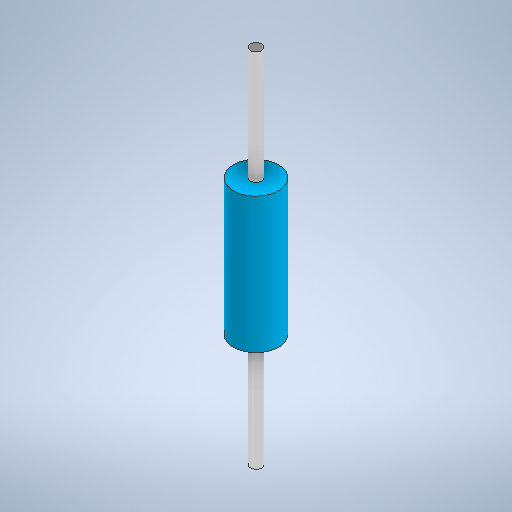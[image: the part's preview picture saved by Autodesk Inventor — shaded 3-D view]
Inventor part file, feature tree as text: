
AUTODESK INVENTOR PART (.ipt)
format: ipt  version: 2025.2 (Build 292293000, 293)  size: 261,120 bytes
history: native  units: mm
features: extrude x3, sketch x3
ambient origin geometry x8: Origin, YZ Plane, XZ Plane, XY Plane, X Axis, Y Axis, Z Axis, Center Point
bodies: Solid1 (feature_tree)
feature tree (6):
  extrude  "Extrusion1"  Depth=6.0mm TaperAngle=0.0deg
  extrude  "Extrusion2"  Depth=5.0mm TaperAngle=0.0deg
  extrude  "Extrusion3"  Depth=5.0mm TaperAngle=0.0deg
  sketch  "Sketch1"  dims[d0=2.0mm d1=6.0mm d2=0.0mm]
  sketch  "Sketch2"  dims[d3=0.5mm d4=5.0mm d5=0.0mm]
  sketch  "Sketch3"  dims[d6=0.5mm d7=5.0mm d8=0.0mm]
